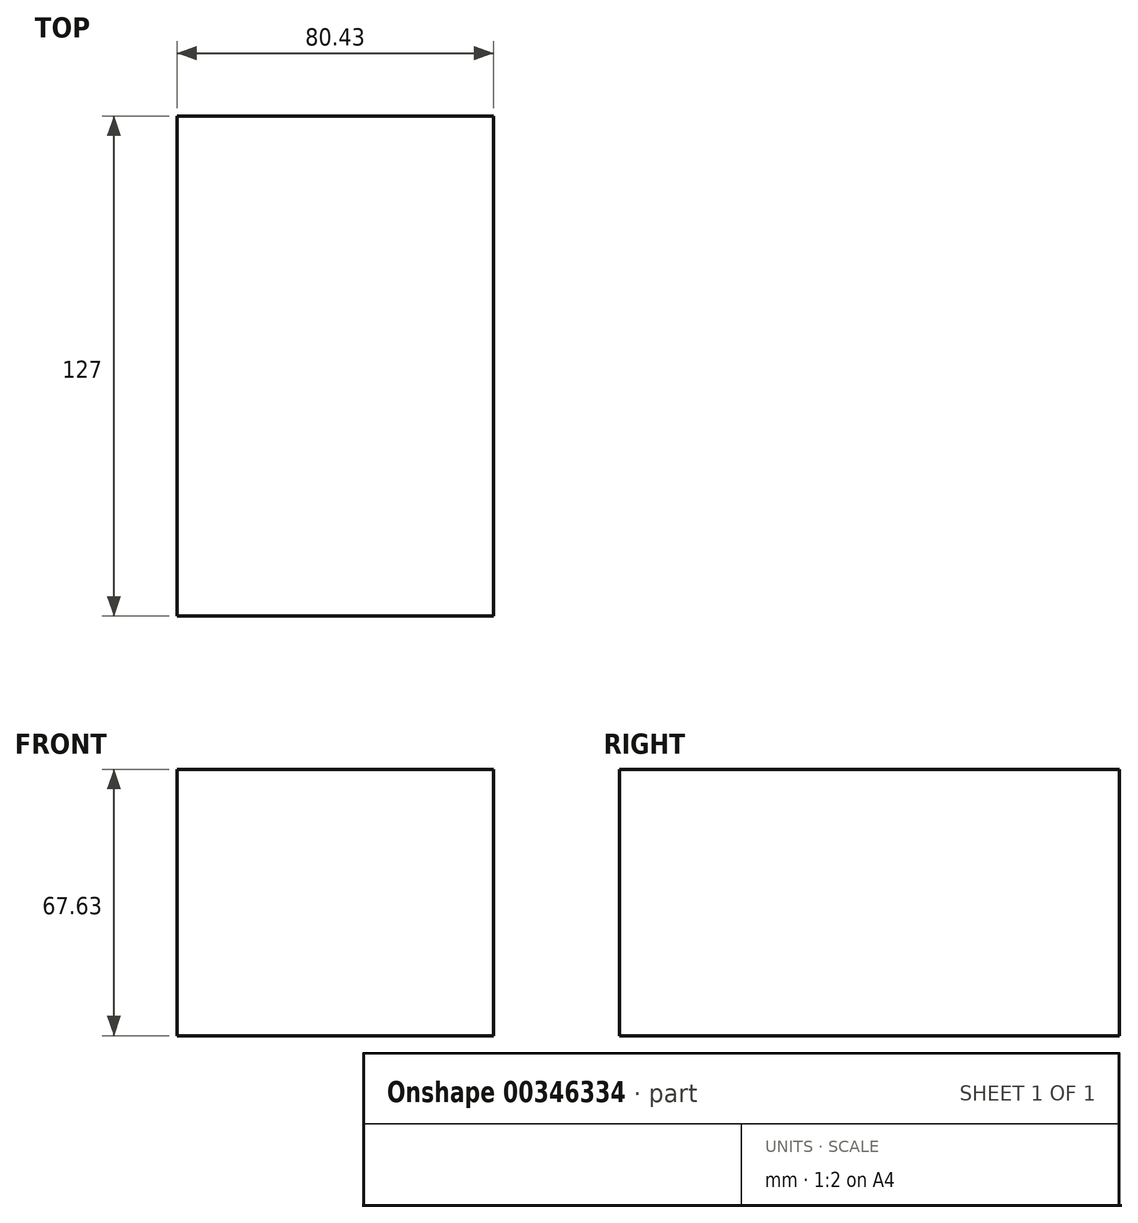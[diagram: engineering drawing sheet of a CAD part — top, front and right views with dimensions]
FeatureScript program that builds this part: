
annotation { "Feature Type Name" : "Feature", "Feature Type Description" : "" }
export const myFeature = defineFeature(function(context is Context, id is Id, definition is map)
    precondition{}
    {
        {
            var Q0;
            Q0=qCreatedBy(makeId("Front.planeOp"),FACE);
            var sketch = newSketch(context, id + "F0", { "sketchPlane" : qUnion([Q0])});
            skLineSegment(sketch, "E0.bottom", {"start": v(-48.34, 50.22) * mm, "end": v(32.09, 50.22) * mm});
            skLineSegment(sketch, "E0.top", {"start": v(-48.34, -17.4) * mm, "end": v(32.09, -17.4) * mm});
            skLineSegment(sketch, "E0.left", {"start": v(-48.34, 50.22) * mm, "end": v(-48.34, -17.4) * mm});
            skLineSegment(sketch, "E0.right", {"start": v(32.09, 50.22) * mm, "end": v(32.09, -17.4) * mm});
            skSolve(sketch);
        }
        {
            var Q0;
            Q0 = qSketchRegion(id + "F0", true);
            extrude(context, id + "F1", {"entities" : qUnion([Q0]), "depth" : 127 * mm});
        }
    });
